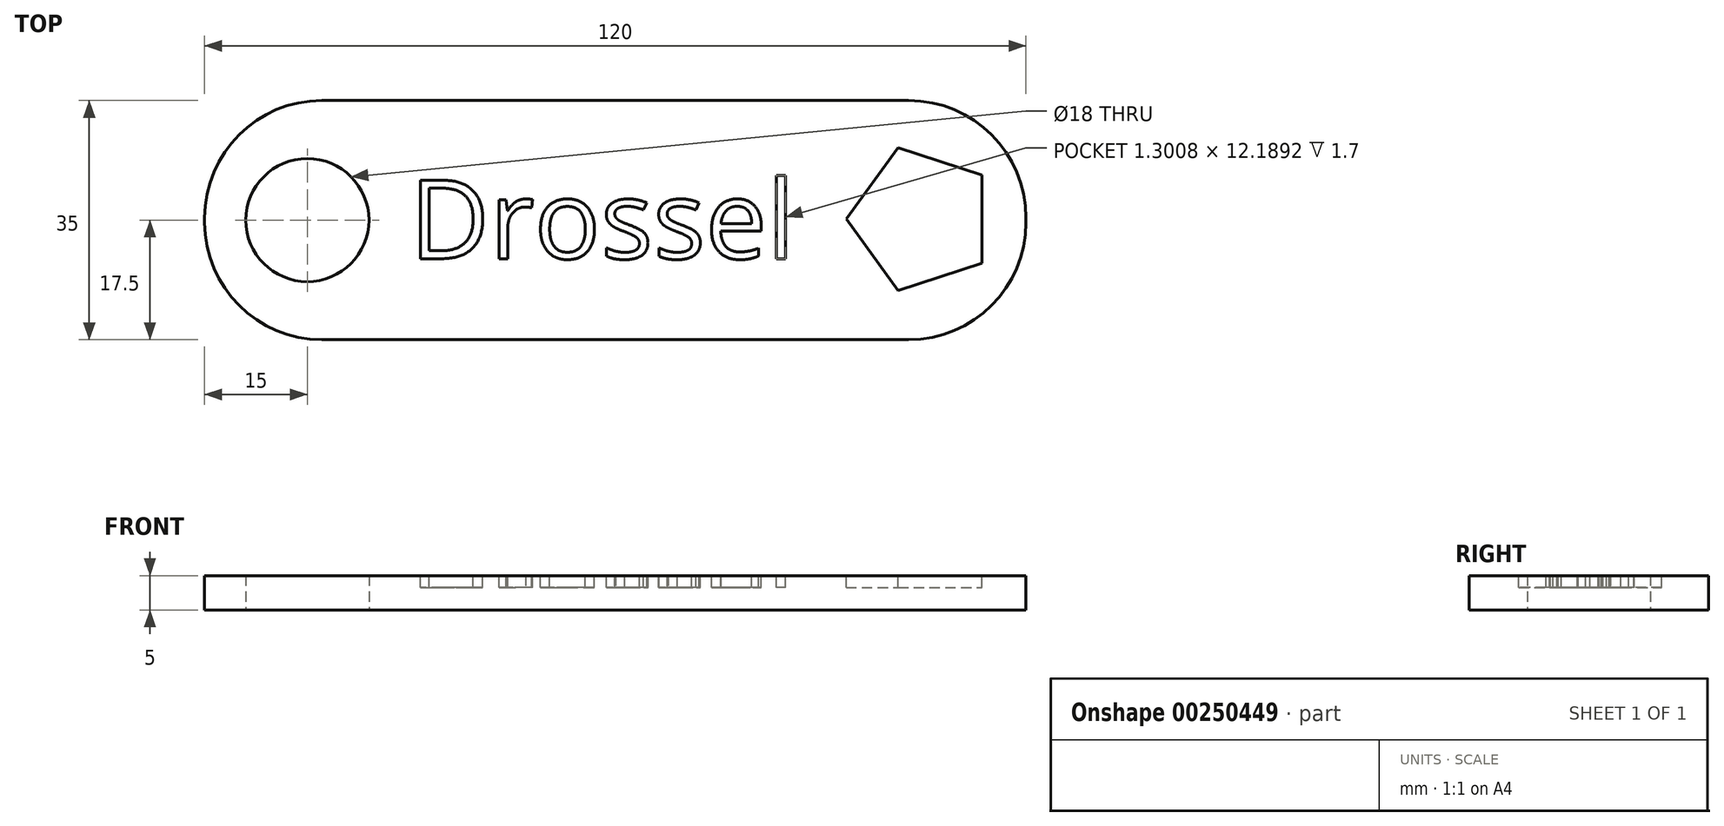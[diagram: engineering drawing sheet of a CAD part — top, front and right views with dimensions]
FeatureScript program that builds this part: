
annotation { "Feature Type Name" : "Feature", "Feature Type Description" : "" }
export const myFeature = defineFeature(function(context is Context, id is Id, definition is map)
    precondition{}
    {
        {
            var Q0;
            Q0=qCreatedBy(makeId("Top.planeOp"),FACE);
            var sketch = newSketch(context, id + "F0", { "sketchPlane" : qUnion([Q0])});
            skLineSegment(sketch, "E0.bottom", {"start": v(-60, 17.5) * mm, "end": v(60, 17.5) * mm});
            skLineSegment(sketch, "E0.top", {"start": v(-60, -17.5) * mm, "end": v(60, -17.5) * mm});
            skLineSegment(sketch, "E0.left", {"start": v(-60, 17.5) * mm, "end": v(-60, -17.5) * mm});
            skLineSegment(sketch, "E0.right", {"start": v(60, 17.5) * mm, "end": v(60, -17.5) * mm});
            skPoint(sketch, "E0.middle", {"position": v(0, 0) * mm});
            skCircle(sketch, "E1", {"center": v(-45, 0) * mm, "radius": 9 * mm});
            skSolve(sketch);
        }
        {
            var Q0;
            Q0=makeQuery(id+"F0.imprint","IMPRINT",FACE,{"disambiguationData":[TD([[makeQuery(id+"F0.imprint","IMPRINT",EDGE,{"derivedFrom":sQuery(id+"F0.wireOp",EDGE,"E0.bottom")}),-1.0]])]});
            extrude(context, id + "F1", {"entities" : qUnion([Q0]), "depth" : 5 * mm});
        }
        {
            var Q0;
            Q0=makeQuery(id+"F1.opExtrude","CAP_FACE",FACE,{"disambiguationData":[OSD([sQuery(id+"F0.wireOp",EDGE,"E0.bottom"),sQuery(id+"F0.wireOp",EDGE,"E0.top"),sQuery(id+"F0.wireOp",EDGE,"E0.left"),sQuery(id+"F0.wireOp",EDGE,"E0.right"),sQuery(id+"F0.wireOp",EDGE,"E1")])],"isStart":false});
            var sketch = newSketch(context, id + "F2", { "sketchPlane" : qUnion([Q0])});
            skText(sketch, "E2", { "text": "Drossel\n", "fontName": "OpenSans-Regular.ttf"});
            skCircle(sketch, "E3.cCircle", {"center": v(44.7, 0.17) * mm, "radius": 8.88 * mm, "construction": true});
            skLineSegment(sketch, "E3.0", {"start": v(53.59, 6.63) * mm, "end": v(53.59, -6.28) * mm});
            skLineSegment(sketch, "E3.1", {"start": v(53.59, -6.28) * mm, "end": v(41.31, -10.27) * mm});
            skLineSegment(sketch, "E3.2", {"start": v(41.31, -10.27) * mm, "end": v(33.73, 0.17) * mm});
            skLineSegment(sketch, "E3.3", {"start": v(33.73, 0.17) * mm, "end": v(41.31, 10.61) * mm});
            skLineSegment(sketch, "E3.4", {"start": v(41.31, 10.61) * mm, "end": v(53.59, 6.63) * mm});
            skPoint(sketch, "E3.0.midPoint", {"position": v(53.59, 0.17) * mm});
            const initialGuessF2  = {"E2": [-0.03008, -0.00563, 1, 0, 0.01155]};
            skSetInitialGuess(sketch, initialGuessF2);
            skSolve(sketch);
        }
        {
            var Q0;
            Q0=makeQuery(id+"F1.opExtrude","SWEPT_EDGE",EDGE,{"disambiguationData":[OSD([sQuery(id+"F0.wireOp",EDGE,"E0.top"),sQuery(id+"F0.wireOp",EDGE,"E0.left")])]});
            var Q1;
            Q1=makeQuery(id+"F1.opExtrude","SWEPT_EDGE",EDGE,{"disambiguationData":[OSD([sQuery(id+"F0.wireOp",EDGE,"E0.bottom"),sQuery(id+"F0.wireOp",EDGE,"E0.right")])]});
            var Q2;
            Q2=makeQuery(id+"F1.opExtrude","SWEPT_EDGE",EDGE,{"disambiguationData":[OSD([sQuery(id+"F0.wireOp",EDGE,"E0.bottom"),sQuery(id+"F0.wireOp",EDGE,"E0.left")])]});
            var Q3;
            Q3=makeQuery(id+"F1.opExtrude","SWEPT_EDGE",EDGE,{"disambiguationData":[OSD([sQuery(id+"F0.wireOp",EDGE,"E0.top"),sQuery(id+"F0.wireOp",EDGE,"E0.right")])]});
            fillet(context, id + "F3", {"entities" : qUnion([Q0, Q1, Q2, Q3]), "radius" : 17.14 * mm, "tangentPropagation" : true, "allowEdgeOverflow" : false});
        }
        {
            var Q0;
            Q0 = qSketchRegion(id + "F2", true);
            extrude(context, id + "F4", {"entities" : qUnion([Q0]), "operationType" : NewBodyOperationType.REMOVE, "oppositeDirection" : true, "depth" : 1.7 * mm});
        }
    });
